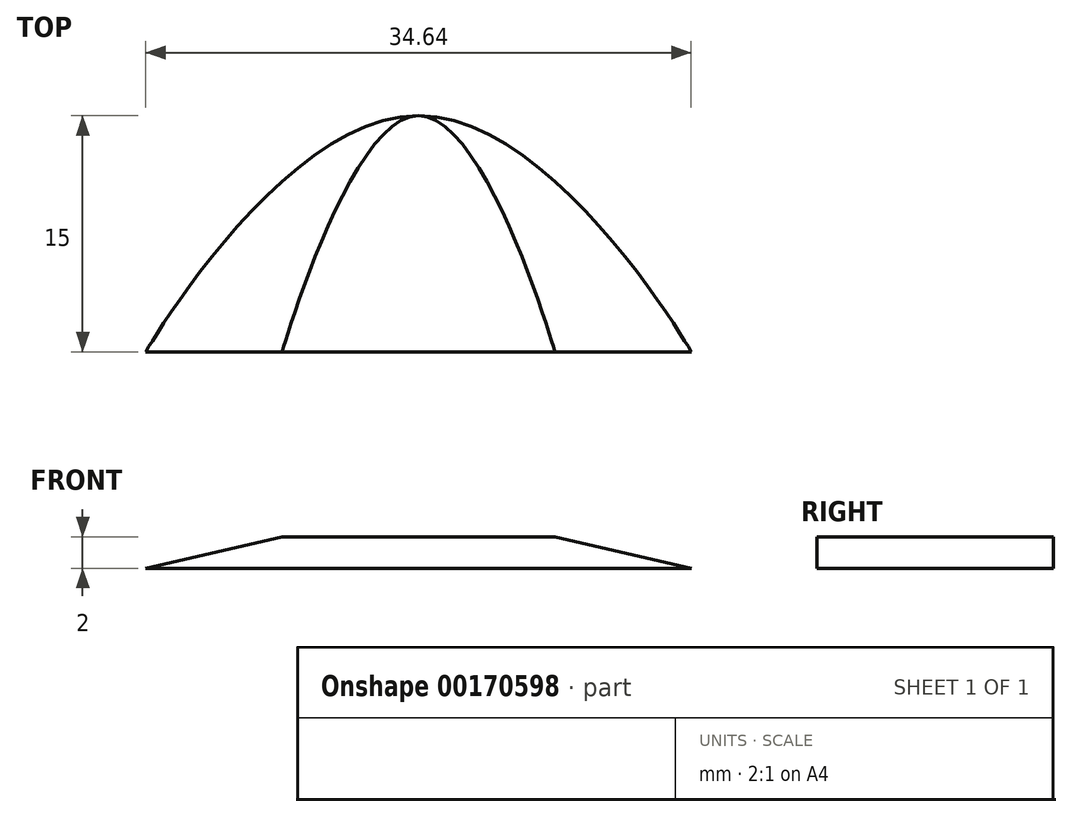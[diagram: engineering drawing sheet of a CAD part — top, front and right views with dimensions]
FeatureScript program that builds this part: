
annotation { "Feature Type Name" : "Feature", "Feature Type Description" : "" }
export const myFeature = defineFeature(function(context is Context, id is Id, definition is map)
    precondition{}
    {
        {
            assignVariable(context, id + "F0", {"name" : "Height", "anyValue" : 2});
        }
        {
            var Q0;
            Q0=qCreatedBy(makeId("Top.planeOp"),FACE);
            var sketch = newSketch(context, id + "F1", { "sketchPlane" : qUnion([Q0])});
            skLineSegment(sketch, "E0", {"start": v(0, 0) * mm, "end": v(34.64, 0) * mm});
            skFitSpline(sketch, "E1", {"points": [v(0, 0) * mm, v(17.32, 15) * mm, v(34.64, 0) * mm], "startDerivative": vector(0, 0.01) * mm, "endDerivative": vector(0, -0.01) * mm});
            skSolve(sketch);
        }
        {
            var Q0;
            Q0=qCreatedBy(makeId("Top.planeOp"),FACE);
            cPlane(context, id + "F2", {"entities" : qUnion([Q0]), "cplaneType" : CPlaneType.OFFSET, "offset" : (getVariable(context, 'Height')) * mm, "width" : 150 * mm, "height" : 150 * mm});
        }
        {
            var Q0;
            Q0=qCreatedBy(id+"F2.planeOp",FACE);
            var sketch = newSketch(context, id + "F3", { "sketchPlane" : qUnion([Q0])});
            skLineSegment(sketch, "E2", {"start": v(8.66, 0) * mm, "end": v(25.98, 0) * mm});
            skFitSpline(sketch, "E3", {"points": [v(8.66, 0) * mm, v(17.32, 15) * mm, v(25.98, 0) * mm], "startDerivative": vector(0, 0.01) * mm, "endDerivative": vector(0, -0.01) * mm});
            skSolve(sketch);
        }
        {
            var Q0;
            Q0=makeQuery(id+"F1.imprint","IMPRINT",FACE,{"disambiguationData":[TD([[makeQuery(id+"F1.imprint","IMPRINT",EDGE,{"derivedFrom":sQuery(id+"F1.wireOp",EDGE,"E0")}),1.0]])]});
            var Q1;
            Q1=qSketchRegion(id+"F3",true);
            loft(context, id + "F4", {"sheetProfilesArray" : [{ "sheetProfileEntities" : qUnion([Q0]) }, { "sheetProfileEntities" : qUnion([Q1]) }]});
        }
    });
